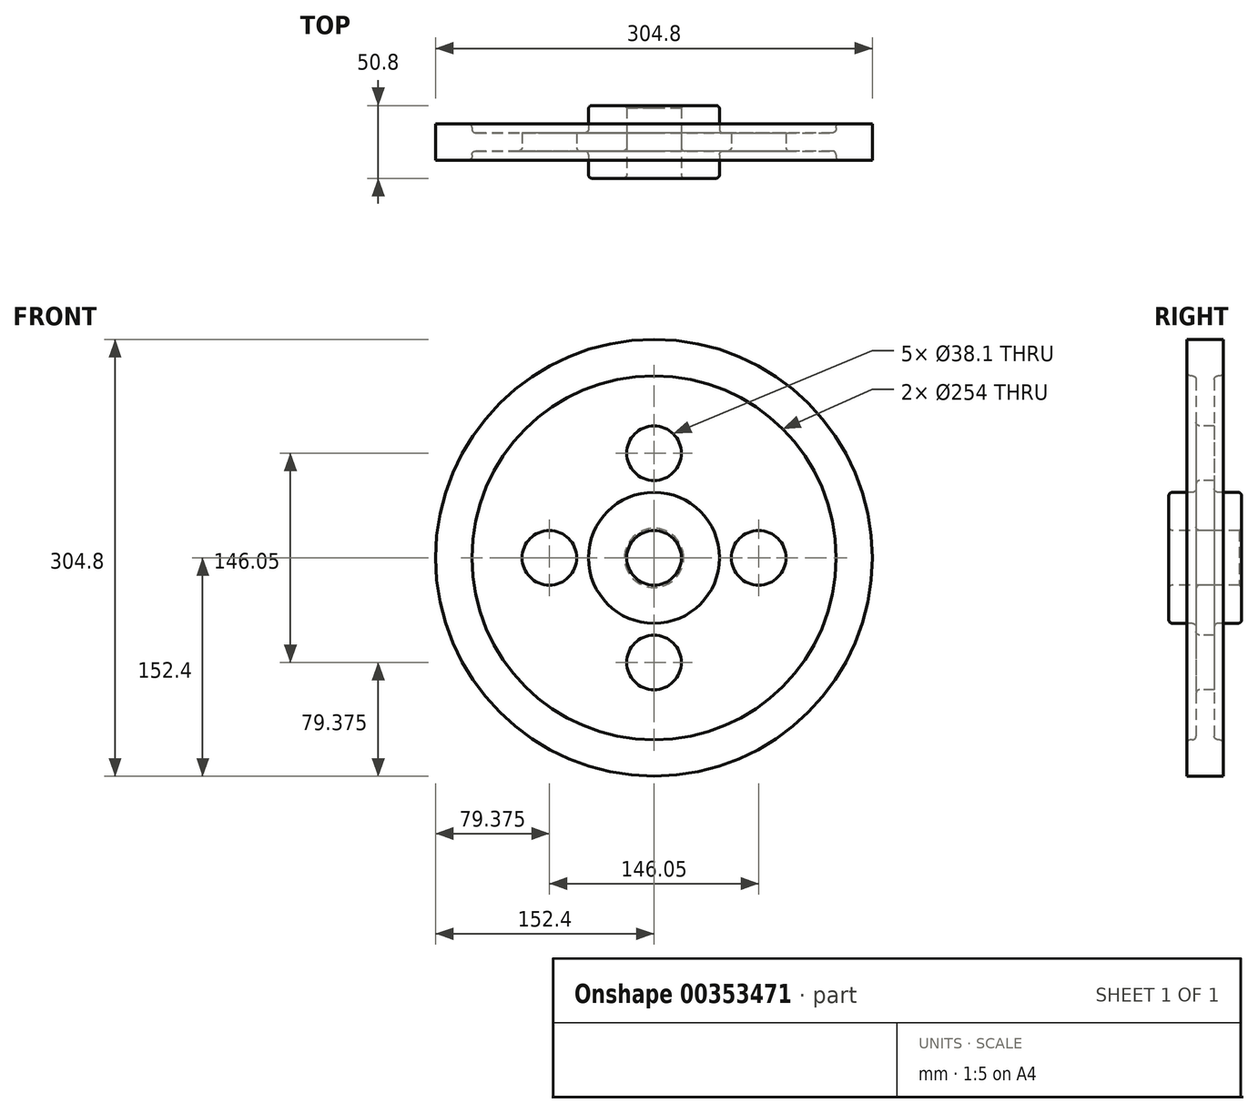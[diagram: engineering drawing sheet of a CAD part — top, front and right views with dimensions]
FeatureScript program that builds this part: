
annotation { "Feature Type Name" : "Feature", "Feature Type Description" : "" }
export const myFeature = defineFeature(function(context is Context, id is Id, definition is map)
    precondition{}
    {
        {
            var Q0;
            Q0=qCreatedBy(makeId("Right.planeOp"),FACE);
            var sketch = newSketch(context, id + "F0", { "sketchPlane" : qUnion([Q0])});
            skLineSegment(sketch, "E0", {"start": v(0, 0) * mm, "end": v(69.5, 0) * mm, "construction": true});
            skLineSegment(sketch, "E1.0", {"start": v(6.35, 26.67) * mm, "end": v(25.4, 26.67) * mm});
            skLineSegment(sketch, "E2.0", {"start": v(6.35, 107.95) * mm, "end": v(12.7, 107.95) * mm});
            skLineSegment(sketch, "E3.0", {"start": v(0, 133.35) * mm, "end": v(12.7, 133.35) * mm});
            skLineSegment(sketch, "E4", {"start": v(0, 133.35) * mm, "end": v(0, 0) * mm, "construction": true});
            skLineSegment(sketch, "E5.0", {"start": v(12.7, 133.35) * mm, "end": v(12.7, 107.95) * mm});
            skLineSegment(sketch, "E6.0", {"start": v(6.35, 107.95) * mm, "end": v(6.35, 26.67) * mm});
            skLineSegment(sketch, "E7.trimOffspring", {"start": v(25.4, 26.67) * mm, "end": v(25.4, 0) * mm});
            skLineSegment(sketch, "E8.MirrorCS", {"start": v(-6.35, 107.95) * mm, "end": v(-6.35, 26.67) * mm});
            skLineSegment(sketch, "E9.MirrorCS", {"start": v(-12.7, 133.35) * mm, "end": v(-12.7, 107.95) * mm});
            skLineSegment(sketch, "E10.MirrorCS", {"start": v(0, 133.35) * mm, "end": v(-12.7, 133.35) * mm});
            skLineSegment(sketch, "E11.MirrorCS", {"start": v(-6.35, 26.67) * mm, "end": v(-25.4, 26.67) * mm});
            skLineSegment(sketch, "E12.MirrorCS", {"start": v(-25.4, 26.67) * mm, "end": v(-25.4, 0) * mm});
            skLineSegment(sketch, "E13.MirrorCS", {"start": v(0, 0) * mm, "end": v(-69.5, 0) * mm, "construction": true});
            skLineSegment(sketch, "E14", {"start": v(-6.35, 107.95) * mm, "end": v(-12.7, 107.95) * mm});
            skLineSegment(sketch, "E15", {"start": v(-25.4, 0) * mm, "end": v(25.4, 0) * mm});
            skLineSegment(sketch, "E16.0", {"start": v(0, -19.05) * mm, "end": v(69.5, -19.05) * mm});
            skSolve(sketch);
        }
        {
            var Q0;
            Q0=makeQuery(id+"F0.imprint","IMPRINT",FACE,{"disambiguationData":[TD([[makeQuery(id+"F0.imprint","IMPRINT",EDGE,{"derivedFrom":sQuery(id+"F0.wireOp",EDGE,"E1.0")}),-1.0]])]});
            var Q1;
            Q1=sQuery(id+"F0.wireOp",EDGE,"E16.0");
            revolve(context, id + "F1", {"entities" : qUnion([Q0]), "axis" : qUnion([Q1]), "revolveType" : RevolveType.FULL});
        }
        {
            var Q0;
            Q0=makeQuery(id+"F1.opRevolve","SWEPT_FACE",FACE,{"disambiguationData":[OSD([sQuery(id+"F0.wireOp",EDGE,"E8.MirrorCS")])]});
            var sketch = newSketch(context, id + "F2", { "sketchPlane" : qUnion([Q0])});
            skLineSegment(sketch, "E17", {"start": v(0, 0) * mm, "end": v(64.46, 0) * mm});
            skLineSegment(sketch, "E18.0", {"start": v(0, -19.05) * mm, "end": v(64.46, -19.05) * mm});
            skLineSegment(sketch, "E19", {"start": v(0, -19.05) * mm, "end": v(0, 53.98) * mm});
            skCircle(sketch, "E20", {"center": v(0, 53.98) * mm, "radius": 19.05 * mm});
            skCircle(sketch, "E21.1.0", {"center": v(-73.03, -19.05) * mm, "radius": 19.05 * mm});
            skCircle(sketch, "E21.2.0", {"center": v(0, -92.08) * mm, "radius": 19.05 * mm});
            skCircle(sketch, "E21.3.0", {"center": v(73.03, -19.05) * mm, "radius": 19.05 * mm});
            skPoint(sketch, "E21.center", {"position": v(0, -19.05) * mm});
            skSolve(sketch);
        }
        {
            var Q0;
            Q0=makeQuery(id+"F2.imprint","IMPRINT",FACE,{"disambiguationData":[TD([[makeQuery(id+"F2.imprint","IMPRINT",EDGE,{"derivedFrom":sQuery(id+"F2.wireOp",EDGE,"E21.3.0")}),1.0]])]});
            var Q1;
            Q1=makeQuery(id+"F2.imprint","IMPRINT",FACE,{"disambiguationData":[TD([[makeQuery(id+"F2.imprint","IMPRINT",EDGE,{"derivedFrom":sQuery(id+"F2.wireOp",EDGE,"E21.1.0")}),1.0]])]});
            var Q2;
            Q2=makeQuery(id+"F2.imprint","IMPRINT",FACE,{"disambiguationData":[TD([[makeQuery(id+"F2.imprint","IMPRINT",EDGE,{"derivedFrom":sQuery(id+"F2.wireOp",EDGE,"E21.2.0")}),1.0]])]});
            var Q3;
            Q3=makeQuery(id+"F2.imprint","IMPRINT",FACE,{"disambiguationData":[TD([[makeQuery(id+"F2.imprint","IMPRINT",EDGE,{"derivedFrom":sQuery(id+"F2.wireOp",EDGE,"E20")}),1.0]])]});
            extrude(context, id + "F3", {"entities" : qUnion([Q0, Q1, Q2, Q3]), "operationType" : NewBodyOperationType.REMOVE, "oppositeDirection" : true, "depth" : 25.4 * mm});
        }
        {
            var Q0;
            Q0=makeQuery(id+"F1.opRevolve","SWEPT_EDGE",EDGE,{"disambiguationData":[OSD([sQuery(id+"F0.wireOp",EDGE,"E9.MirrorCS"),sQuery(id+"F0.wireOp",EDGE,"E14")])]});
            var Q1;
            Q1=makeQuery(id+"F1.opRevolve","SWEPT_EDGE",EDGE,{"disambiguationData":[OSD([sQuery(id+"F0.wireOp",EDGE,"E8.MirrorCS"),sQuery(id+"F0.wireOp",EDGE,"E14")])]});
            var Q2;
            Q2=makeQuery(id+"F1.opRevolve","SWEPT_FACE",FACE,{"disambiguationData":[OSD([sQuery(id+"F0.wireOp",EDGE,"E12.MirrorCS")])]});
            var Q3;
            Q3=makeQuery(id+"F1.opRevolve","SWEPT_FACE",FACE,{"disambiguationData":[OSD([sQuery(id+"F0.wireOp",EDGE,"E8.MirrorCS")])]});
            fillet(context, id + "F4", {"entities" : qUnion([Q0, Q1, Q2, Q3]), "radius" : 2.54 * mm, "tangentPropagation" : true, "allowEdgeOverflow" : false});
        }
        {
            var Q0;
            {var subQ0=sQuery(id+"F0.wireOp",EDGE,"E12.MirrorCS");Q0=makeQuery(id+"F4.opFillet","BLEND_EDGE",EDGE,{"blendedFrom":[makeQuery(id+"F1.opRevolve","SWEPT_EDGE",EDGE,{"disambiguationData":[OSD([subQ0,sQuery(id+"F0.wireOp",EDGE,"E15")])]}),makeQuery(id+"F1.opRevolve","SWEPT_FACE",FACE,{"disambiguationData":[OSD([subQ0])]})],"blendedInto":[makeQuery(id+"F1.opRevolve","SWEPT_FACE",FACE,{"disambiguationData":[OSD([subQ0])]})]});}
            var Q1;
            Q1=makeQuery(id+"F1.opRevolve","SWEPT_EDGE",EDGE,{"disambiguationData":[OSD([sQuery(id+"F0.wireOp",EDGE,"E7.trimOffspring"),sQuery(id+"F0.wireOp",EDGE,"E15")])]});
            chamfer(context, id + "F5", {"entities" : qUnion([Q0, Q1]), "width" : 1.59 * mm, "tangentPropagation" : true});
        }
        {
            var Q0;
            Q0=makeQuery(id+"F1.opRevolve","SWEPT_EDGE",EDGE,{"disambiguationData":[OSD([sQuery(id+"F0.wireOp",EDGE,"E2.0"),sQuery(id+"F0.wireOp",EDGE,"E6.0")])]});
            var Q1;
            Q1=makeQuery(id+"F1.opRevolve","SWEPT_EDGE",EDGE,{"disambiguationData":[OSD([sQuery(id+"F0.wireOp",EDGE,"E2.0"),sQuery(id+"F0.wireOp",EDGE,"E5.0")])]});
            var Q2;
            Q2=makeQuery(id+"F1.opRevolve","SWEPT_EDGE",EDGE,{"disambiguationData":[OSD([sQuery(id+"F0.wireOp",EDGE,"E1.0"),sQuery(id+"F0.wireOp",EDGE,"E7.trimOffspring")])]});
            var Q3;
            Q3=makeQuery(id+"F1.opRevolve","SWEPT_EDGE",EDGE,{"disambiguationData":[OSD([sQuery(id+"F0.wireOp",EDGE,"E1.0"),sQuery(id+"F0.wireOp",EDGE,"E6.0")])]});
            fillet(context, id + "F6", {"entities" : qUnion([Q0, Q1, Q2, Q3]), "radius" : 2.54 * mm, "tangentPropagation" : true, "allowEdgeOverflow" : false});
        }
    });
